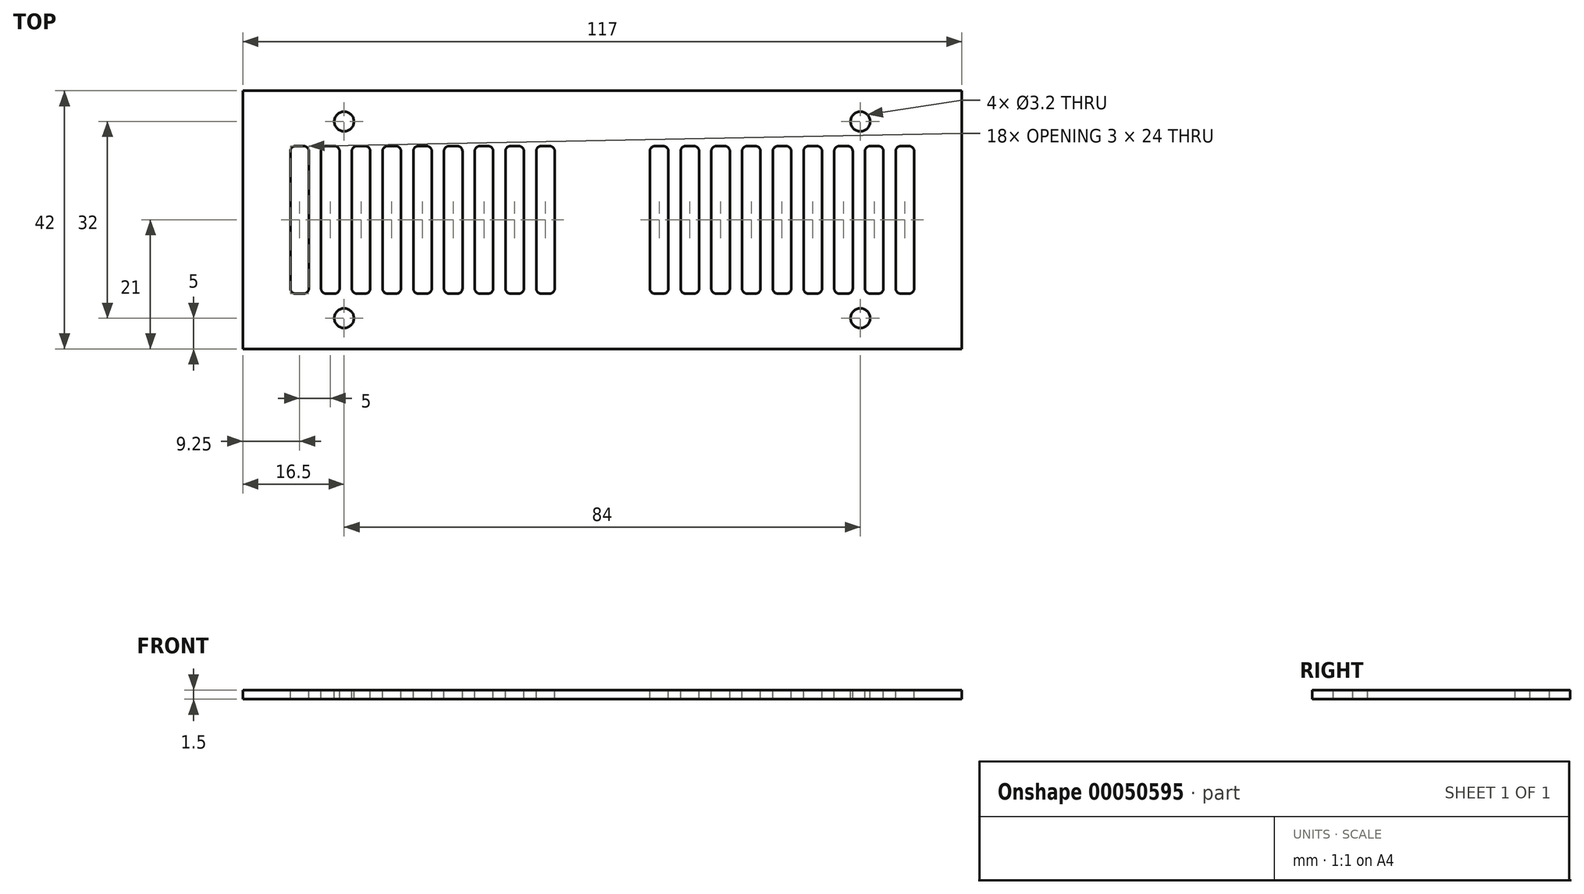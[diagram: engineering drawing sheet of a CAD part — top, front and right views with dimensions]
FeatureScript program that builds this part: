
annotation { "Feature Type Name" : "Feature", "Feature Type Description" : "" }
export const myFeature = defineFeature(function(context is Context, id is Id, definition is map)
    precondition{}
    {
        {
            var Q0;
            Q0=qCreatedBy(makeId("Top.planeOp"),FACE);
            var sketch = newSketch(context, id + "F0", { "sketchPlane" : qUnion([Q0])});
            skLineSegment(sketch, "E0.rect.bottom", {"start": v(58.5, 21) * mm, "end": v(-58.5, 21) * mm});
            skLineSegment(sketch, "E0.rect.top", {"start": v(58.5, -21) * mm, "end": v(-58.5, -21) * mm});
            skLineSegment(sketch, "E0.rect.left", {"start": v(58.5, 21) * mm, "end": v(58.5, -21) * mm});
            skLineSegment(sketch, "E0.rect.right", {"start": v(-58.5, 21) * mm, "end": v(-58.5, -21) * mm});
            skPoint(sketch, "E0.rect.middle", {"position": v(0, 0) * mm});
            skCircle(sketch, "E1", {"center": v(-42, 16) * mm, "radius": 1.6 * mm});
            skCircle(sketch, "E2", {"center": v(42, 16) * mm, "radius": 1.6 * mm});
            skCircle(sketch, "E3", {"center": v(-42, -16) * mm, "radius": 1.6 * mm});
            skCircle(sketch, "E4", {"center": v(42, -16) * mm, "radius": 1.6 * mm});
            skLineSegment(sketch, "E5.rect.bottom", {"start": v(8.55, 12) * mm, "end": v(9.95, 12) * mm});
            skLineSegment(sketch, "E5.rect.top", {"start": v(8.55, -12) * mm, "end": v(9.95, -12) * mm});
            skLineSegment(sketch, "E5.rect.left", {"start": v(7.75, 11.2) * mm, "end": v(7.75, -11.2) * mm});
            skLineSegment(sketch, "E5.rect.right", {"start": v(10.75, 11.2) * mm, "end": v(10.75, -11.2) * mm});
            skPoint(sketch, "E5.rect.middle", {"position": v(9.25, 0) * mm});
            skPoint(sketch, "E6.visualSharp", {"position": v(7.75, 12) * mm});
            skArc(sketch, "E6.filletArc", {"start": v(8.55, 12) * mm, "mid": v(7.98, 11.77) * mm, "end": v(7.75, 11.2) * mm});
            skPoint(sketch, "E7.visualSharp", {"position": v(10.75, 12) * mm});
            skArc(sketch, "E7.filletArc", {"start": v(10.75, 11.2) * mm, "mid": v(10.52, 11.77) * mm, "end": v(9.95, 12) * mm});
            skPoint(sketch, "E8.visualSharp", {"position": v(10.75, -12) * mm});
            skArc(sketch, "E8.filletArc", {"start": v(9.95, -12) * mm, "mid": v(10.52, -11.77) * mm, "end": v(10.75, -11.2) * mm});
            skPoint(sketch, "E9.visualSharp", {"position": v(7.75, -12) * mm});
            skArc(sketch, "E9.filletArc", {"start": v(7.75, -11.2) * mm, "mid": v(7.98, -11.77) * mm, "end": v(8.55, -12) * mm});
            skPoint(sketch, "E10.1.0.0", {"position": v(14.25, 0) * mm});
            skPoint(sketch, "E10.1.0.1", {"position": v(12.75, -12) * mm});
            skPoint(sketch, "E10.1.0.2", {"position": v(15.75, -12) * mm});
            skPoint(sketch, "E10.1.0.3", {"position": v(15.75, 12) * mm});
            skLineSegment(sketch, "E10.1.0.4", {"start": v(12.75, 11.2) * mm, "end": v(12.75, -11.2) * mm});
            skLineSegment(sketch, "E10.1.0.5", {"start": v(15.75, 11.2) * mm, "end": v(15.75, -11.2) * mm});
            skPoint(sketch, "E10.1.0.6", {"position": v(12.75, 12) * mm});
            skArc(sketch, "E10.1.0.7", {"start": v(12.75, -11.2) * mm, "mid": v(12.98, -11.77) * mm, "end": v(13.55, -12) * mm});
            skArc(sketch, "E10.1.0.8", {"start": v(14.95, -12) * mm, "mid": v(15.52, -11.77) * mm, "end": v(15.75, -11.2) * mm});
            skArc(sketch, "E10.1.0.9", {"start": v(15.75, 11.2) * mm, "mid": v(15.52, 11.77) * mm, "end": v(14.95, 12) * mm});
            skLineSegment(sketch, "E10.1.0.10", {"start": v(13.55, 12) * mm, "end": v(14.95, 12) * mm});
            skLineSegment(sketch, "E10.1.0.11", {"start": v(13.55, -12) * mm, "end": v(14.95, -12) * mm});
            skArc(sketch, "E10.1.0.12", {"start": v(13.55, 12) * mm, "mid": v(12.98, 11.77) * mm, "end": v(12.75, 11.2) * mm});
            skPoint(sketch, "E10.2.0.0", {"position": v(19.25, 0) * mm});
            skPoint(sketch, "E10.2.0.1", {"position": v(17.75, -12) * mm});
            skPoint(sketch, "E10.2.0.2", {"position": v(20.75, -12) * mm});
            skPoint(sketch, "E10.2.0.3", {"position": v(20.75, 12) * mm});
            skLineSegment(sketch, "E10.2.0.4", {"start": v(17.75, 11.2) * mm, "end": v(17.75, -11.2) * mm});
            skLineSegment(sketch, "E10.2.0.5", {"start": v(20.75, 11.2) * mm, "end": v(20.75, -11.2) * mm});
            skPoint(sketch, "E10.2.0.6", {"position": v(17.75, 12) * mm});
            skArc(sketch, "E10.2.0.7", {"start": v(17.75, -11.2) * mm, "mid": v(17.98, -11.77) * mm, "end": v(18.55, -12) * mm});
            skArc(sketch, "E10.2.0.8", {"start": v(19.95, -12) * mm, "mid": v(20.52, -11.77) * mm, "end": v(20.75, -11.2) * mm});
            skArc(sketch, "E10.2.0.9", {"start": v(20.75, 11.2) * mm, "mid": v(20.52, 11.77) * mm, "end": v(19.95, 12) * mm});
            skLineSegment(sketch, "E10.2.0.10", {"start": v(18.55, 12) * mm, "end": v(19.95, 12) * mm});
            skLineSegment(sketch, "E10.2.0.11", {"start": v(18.55, -12) * mm, "end": v(19.95, -12) * mm});
            skArc(sketch, "E10.2.0.12", {"start": v(18.55, 12) * mm, "mid": v(17.98, 11.77) * mm, "end": v(17.75, 11.2) * mm});
            skPoint(sketch, "E10.3.0.0", {"position": v(24.25, 0) * mm});
            skPoint(sketch, "E10.3.0.1", {"position": v(22.75, -12) * mm});
            skPoint(sketch, "E10.3.0.2", {"position": v(25.75, -12) * mm});
            skPoint(sketch, "E10.3.0.3", {"position": v(25.75, 12) * mm});
            skLineSegment(sketch, "E10.3.0.4", {"start": v(22.75, 11.2) * mm, "end": v(22.75, -11.2) * mm});
            skLineSegment(sketch, "E10.3.0.5", {"start": v(25.75, 11.2) * mm, "end": v(25.75, -11.2) * mm});
            skPoint(sketch, "E10.3.0.6", {"position": v(22.75, 12) * mm});
            skArc(sketch, "E10.3.0.7", {"start": v(22.75, -11.2) * mm, "mid": v(22.98, -11.77) * mm, "end": v(23.55, -12) * mm});
            skArc(sketch, "E10.3.0.8", {"start": v(24.95, -12) * mm, "mid": v(25.52, -11.77) * mm, "end": v(25.75, -11.2) * mm});
            skArc(sketch, "E10.3.0.9", {"start": v(25.75, 11.2) * mm, "mid": v(25.52, 11.77) * mm, "end": v(24.95, 12) * mm});
            skLineSegment(sketch, "E10.3.0.10", {"start": v(23.55, 12) * mm, "end": v(24.95, 12) * mm});
            skLineSegment(sketch, "E10.3.0.11", {"start": v(23.55, -12) * mm, "end": v(24.95, -12) * mm});
            skArc(sketch, "E10.3.0.12", {"start": v(23.55, 12) * mm, "mid": v(22.98, 11.77) * mm, "end": v(22.75, 11.2) * mm});
            skPoint(sketch, "E10.4.0.0", {"position": v(29.25, 0) * mm});
            skPoint(sketch, "E10.4.0.1", {"position": v(27.75, -12) * mm});
            skPoint(sketch, "E10.4.0.2", {"position": v(30.75, -12) * mm});
            skPoint(sketch, "E10.4.0.3", {"position": v(30.75, 12) * mm});
            skLineSegment(sketch, "E10.4.0.4", {"start": v(27.75, 11.2) * mm, "end": v(27.75, -11.2) * mm});
            skLineSegment(sketch, "E10.4.0.5", {"start": v(30.75, 11.2) * mm, "end": v(30.75, -11.2) * mm});
            skPoint(sketch, "E10.4.0.6", {"position": v(27.75, 12) * mm});
            skArc(sketch, "E10.4.0.7", {"start": v(27.75, -11.2) * mm, "mid": v(27.98, -11.77) * mm, "end": v(28.55, -12) * mm});
            skArc(sketch, "E10.4.0.8", {"start": v(29.95, -12) * mm, "mid": v(30.52, -11.77) * mm, "end": v(30.75, -11.2) * mm});
            skArc(sketch, "E10.4.0.9", {"start": v(30.75, 11.2) * mm, "mid": v(30.52, 11.77) * mm, "end": v(29.95, 12) * mm});
            skLineSegment(sketch, "E10.4.0.10", {"start": v(28.55, 12) * mm, "end": v(29.95, 12) * mm});
            skLineSegment(sketch, "E10.4.0.11", {"start": v(28.55, -12) * mm, "end": v(29.95, -12) * mm});
            skArc(sketch, "E10.4.0.12", {"start": v(28.55, 12) * mm, "mid": v(27.98, 11.77) * mm, "end": v(27.75, 11.2) * mm});
            skPoint(sketch, "E10.5.0.0", {"position": v(34.25, 0) * mm});
            skPoint(sketch, "E10.5.0.1", {"position": v(32.75, -12) * mm});
            skPoint(sketch, "E10.5.0.2", {"position": v(35.75, -12) * mm});
            skPoint(sketch, "E10.5.0.3", {"position": v(35.75, 12) * mm});
            skLineSegment(sketch, "E10.5.0.4", {"start": v(32.75, 11.2) * mm, "end": v(32.75, -11.2) * mm});
            skLineSegment(sketch, "E10.5.0.5", {"start": v(35.75, 11.2) * mm, "end": v(35.75, -11.2) * mm});
            skPoint(sketch, "E10.5.0.6", {"position": v(32.75, 12) * mm});
            skArc(sketch, "E10.5.0.7", {"start": v(32.75, -11.2) * mm, "mid": v(32.98, -11.77) * mm, "end": v(33.55, -12) * mm});
            skArc(sketch, "E10.5.0.8", {"start": v(34.95, -12) * mm, "mid": v(35.52, -11.77) * mm, "end": v(35.75, -11.2) * mm});
            skArc(sketch, "E10.5.0.9", {"start": v(35.75, 11.2) * mm, "mid": v(35.52, 11.77) * mm, "end": v(34.95, 12) * mm});
            skLineSegment(sketch, "E10.5.0.10", {"start": v(33.55, 12) * mm, "end": v(34.95, 12) * mm});
            skLineSegment(sketch, "E10.5.0.11", {"start": v(33.55, -12) * mm, "end": v(34.95, -12) * mm});
            skArc(sketch, "E10.5.0.12", {"start": v(33.55, 12) * mm, "mid": v(32.98, 11.77) * mm, "end": v(32.75, 11.2) * mm});
            skPoint(sketch, "E10.6.0.0", {"position": v(39.25, 0) * mm});
            skPoint(sketch, "E10.6.0.1", {"position": v(37.75, -12) * mm});
            skPoint(sketch, "E10.6.0.2", {"position": v(40.75, -12) * mm});
            skPoint(sketch, "E10.6.0.3", {"position": v(40.75, 12) * mm});
            skLineSegment(sketch, "E10.6.0.4", {"start": v(37.75, 11.2) * mm, "end": v(37.75, -11.2) * mm});
            skLineSegment(sketch, "E10.6.0.5", {"start": v(40.75, 11.2) * mm, "end": v(40.75, -11.2) * mm});
            skPoint(sketch, "E10.6.0.6", {"position": v(37.75, 12) * mm});
            skArc(sketch, "E10.6.0.7", {"start": v(37.75, -11.2) * mm, "mid": v(37.98, -11.77) * mm, "end": v(38.55, -12) * mm});
            skArc(sketch, "E10.6.0.8", {"start": v(39.95, -12) * mm, "mid": v(40.52, -11.77) * mm, "end": v(40.75, -11.2) * mm});
            skArc(sketch, "E10.6.0.9", {"start": v(40.75, 11.2) * mm, "mid": v(40.52, 11.77) * mm, "end": v(39.95, 12) * mm});
            skLineSegment(sketch, "E10.6.0.10", {"start": v(38.55, 12) * mm, "end": v(39.95, 12) * mm});
            skLineSegment(sketch, "E10.6.0.11", {"start": v(38.55, -12) * mm, "end": v(39.95, -12) * mm});
            skArc(sketch, "E10.6.0.12", {"start": v(38.55, 12) * mm, "mid": v(37.98, 11.77) * mm, "end": v(37.75, 11.2) * mm});
            skPoint(sketch, "E10.7.0.0", {"position": v(44.25, 0) * mm});
            skPoint(sketch, "E10.7.0.1", {"position": v(42.75, -12) * mm});
            skPoint(sketch, "E10.7.0.2", {"position": v(45.75, -12) * mm});
            skPoint(sketch, "E10.7.0.3", {"position": v(45.75, 12) * mm});
            skLineSegment(sketch, "E10.7.0.4", {"start": v(42.75, 11.2) * mm, "end": v(42.75, -11.2) * mm});
            skLineSegment(sketch, "E10.7.0.5", {"start": v(45.75, 11.2) * mm, "end": v(45.75, -11.2) * mm});
            skPoint(sketch, "E10.7.0.6", {"position": v(42.75, 12) * mm});
            skArc(sketch, "E10.7.0.7", {"start": v(42.75, -11.2) * mm, "mid": v(42.98, -11.77) * mm, "end": v(43.55, -12) * mm});
            skArc(sketch, "E10.7.0.8", {"start": v(44.95, -12) * mm, "mid": v(45.52, -11.77) * mm, "end": v(45.75, -11.2) * mm});
            skArc(sketch, "E10.7.0.9", {"start": v(45.75, 11.2) * mm, "mid": v(45.52, 11.77) * mm, "end": v(44.95, 12) * mm});
            skLineSegment(sketch, "E10.7.0.10", {"start": v(43.55, 12) * mm, "end": v(44.95, 12) * mm});
            skLineSegment(sketch, "E10.7.0.11", {"start": v(43.55, -12) * mm, "end": v(44.95, -12) * mm});
            skArc(sketch, "E10.7.0.12", {"start": v(43.55, 12) * mm, "mid": v(42.98, 11.77) * mm, "end": v(42.75, 11.2) * mm});
            skPoint(sketch, "E10.8.0.0", {"position": v(49.25, 0) * mm});
            skPoint(sketch, "E10.8.0.1", {"position": v(47.75, -12) * mm});
            skPoint(sketch, "E10.8.0.2", {"position": v(50.75, -12) * mm});
            skPoint(sketch, "E10.8.0.3", {"position": v(50.75, 12) * mm});
            skLineSegment(sketch, "E10.8.0.4", {"start": v(47.75, 11.2) * mm, "end": v(47.75, -11.2) * mm});
            skLineSegment(sketch, "E10.8.0.5", {"start": v(50.75, 11.2) * mm, "end": v(50.75, -11.2) * mm});
            skPoint(sketch, "E10.8.0.6", {"position": v(47.75, 12) * mm});
            skArc(sketch, "E10.8.0.7", {"start": v(47.75, -11.2) * mm, "mid": v(47.98, -11.77) * mm, "end": v(48.55, -12) * mm});
            skArc(sketch, "E10.8.0.8", {"start": v(49.95, -12) * mm, "mid": v(50.52, -11.77) * mm, "end": v(50.75, -11.2) * mm});
            skArc(sketch, "E10.8.0.9", {"start": v(50.75, 11.2) * mm, "mid": v(50.52, 11.77) * mm, "end": v(49.95, 12) * mm});
            skLineSegment(sketch, "E10.8.0.10", {"start": v(48.55, 12) * mm, "end": v(49.95, 12) * mm});
            skLineSegment(sketch, "E10.8.0.11", {"start": v(48.55, -12) * mm, "end": v(49.95, -12) * mm});
            skArc(sketch, "E10.8.0.12", {"start": v(48.55, 12) * mm, "mid": v(47.98, 11.77) * mm, "end": v(47.75, 11.2) * mm});
            skLineSegment(sketch, "E10.direction1", {"start": v(9.25, 0) * mm, "end": v(14.25, 0) * mm, "construction": true});
            skLineSegment(sketch, "E11.rect.bottom", {"start": v(-49.95, 12) * mm, "end": v(-48.55, 12) * mm});
            skLineSegment(sketch, "E11.rect.top", {"start": v(-49.95, -12) * mm, "end": v(-48.55, -12) * mm});
            skLineSegment(sketch, "E11.rect.left", {"start": v(-50.75, 11.2) * mm, "end": v(-50.75, -11.2) * mm});
            skLineSegment(sketch, "E11.rect.right", {"start": v(-47.75, 11.2) * mm, "end": v(-47.75, -11.2) * mm});
            skPoint(sketch, "E11.rect.middle", {"position": v(-49.25, 0) * mm});
            skPoint(sketch, "E12.visualSharp", {"position": v(-50.75, 12) * mm});
            skArc(sketch, "E12.filletArc", {"start": v(-49.95, 12) * mm, "mid": v(-50.52, 11.77) * mm, "end": v(-50.75, 11.2) * mm});
            skPoint(sketch, "E13.visualSharp", {"position": v(-47.75, 12) * mm});
            skArc(sketch, "E13.filletArc", {"start": v(-47.75, 11.2) * mm, "mid": v(-47.98, 11.77) * mm, "end": v(-48.55, 12) * mm});
            skPoint(sketch, "E14.visualSharp", {"position": v(-47.75, -12) * mm});
            skArc(sketch, "E14.filletArc", {"start": v(-48.55, -12) * mm, "mid": v(-47.98, -11.77) * mm, "end": v(-47.75, -11.2) * mm});
            skPoint(sketch, "E15.visualSharp", {"position": v(-50.75, -12) * mm});
            skArc(sketch, "E15.filletArc", {"start": v(-50.75, -11.2) * mm, "mid": v(-50.52, -11.77) * mm, "end": v(-49.95, -12) * mm});
            skPoint(sketch, "E16.1.0.0", {"position": v(-42.75, 12) * mm});
            skPoint(sketch, "E16.1.0.1", {"position": v(-42.75, -12) * mm});
            skLineSegment(sketch, "E16.1.0.2", {"start": v(-42.75, 11.2) * mm, "end": v(-42.75, -11.2) * mm});
            skLineSegment(sketch, "E16.1.0.3", {"start": v(-45.75, 11.2) * mm, "end": v(-45.75, -11.2) * mm});
            skPoint(sketch, "E16.1.0.4", {"position": v(-45.75, -12) * mm});
            skPoint(sketch, "E16.1.0.5", {"position": v(-44.25, 0) * mm});
            skPoint(sketch, "E16.1.0.6", {"position": v(-45.75, 12) * mm});
            skArc(sketch, "E16.1.0.7", {"start": v(-44.95, 12) * mm, "mid": v(-45.52, 11.77) * mm, "end": v(-45.75, 11.2) * mm});
            skArc(sketch, "E16.1.0.8", {"start": v(-45.75, -11.2) * mm, "mid": v(-45.52, -11.77) * mm, "end": v(-44.95, -12) * mm});
            skLineSegment(sketch, "E16.1.0.9", {"start": v(-44.95, 12) * mm, "end": v(-43.55, 12) * mm});
            skLineSegment(sketch, "E16.1.0.10", {"start": v(-44.95, -12) * mm, "end": v(-43.55, -12) * mm});
            skArc(sketch, "E16.1.0.11", {"start": v(-42.75, 11.2) * mm, "mid": v(-42.98, 11.77) * mm, "end": v(-43.55, 12) * mm});
            skArc(sketch, "E16.1.0.12", {"start": v(-43.55, -12) * mm, "mid": v(-42.98, -11.77) * mm, "end": v(-42.75, -11.2) * mm});
            skPoint(sketch, "E16.2.0.0", {"position": v(-37.75, 12) * mm});
            skPoint(sketch, "E16.2.0.1", {"position": v(-37.75, -12) * mm});
            skLineSegment(sketch, "E16.2.0.2", {"start": v(-37.75, 11.2) * mm, "end": v(-37.75, -11.2) * mm});
            skLineSegment(sketch, "E16.2.0.3", {"start": v(-40.75, 11.2) * mm, "end": v(-40.75, -11.2) * mm});
            skPoint(sketch, "E16.2.0.4", {"position": v(-40.75, -12) * mm});
            skPoint(sketch, "E16.2.0.5", {"position": v(-39.25, 0) * mm});
            skPoint(sketch, "E16.2.0.6", {"position": v(-40.75, 12) * mm});
            skArc(sketch, "E16.2.0.7", {"start": v(-39.95, 12) * mm, "mid": v(-40.52, 11.77) * mm, "end": v(-40.75, 11.2) * mm});
            skArc(sketch, "E16.2.0.8", {"start": v(-40.75, -11.2) * mm, "mid": v(-40.52, -11.77) * mm, "end": v(-39.95, -12) * mm});
            skLineSegment(sketch, "E16.2.0.9", {"start": v(-39.95, 12) * mm, "end": v(-38.55, 12) * mm});
            skLineSegment(sketch, "E16.2.0.10", {"start": v(-39.95, -12) * mm, "end": v(-38.55, -12) * mm});
            skArc(sketch, "E16.2.0.11", {"start": v(-37.75, 11.2) * mm, "mid": v(-37.98, 11.77) * mm, "end": v(-38.55, 12) * mm});
            skArc(sketch, "E16.2.0.12", {"start": v(-38.55, -12) * mm, "mid": v(-37.98, -11.77) * mm, "end": v(-37.75, -11.2) * mm});
            skPoint(sketch, "E16.3.0.0", {"position": v(-32.75, 12) * mm});
            skPoint(sketch, "E16.3.0.1", {"position": v(-32.75, -12) * mm});
            skLineSegment(sketch, "E16.3.0.2", {"start": v(-32.75, 11.2) * mm, "end": v(-32.75, -11.2) * mm});
            skLineSegment(sketch, "E16.3.0.3", {"start": v(-35.75, 11.2) * mm, "end": v(-35.75, -11.2) * mm});
            skPoint(sketch, "E16.3.0.4", {"position": v(-35.75, -12) * mm});
            skPoint(sketch, "E16.3.0.5", {"position": v(-34.25, 0) * mm});
            skPoint(sketch, "E16.3.0.6", {"position": v(-35.75, 12) * mm});
            skArc(sketch, "E16.3.0.7", {"start": v(-34.95, 12) * mm, "mid": v(-35.52, 11.77) * mm, "end": v(-35.75, 11.2) * mm});
            skArc(sketch, "E16.3.0.8", {"start": v(-35.75, -11.2) * mm, "mid": v(-35.52, -11.77) * mm, "end": v(-34.95, -12) * mm});
            skLineSegment(sketch, "E16.3.0.9", {"start": v(-34.95, 12) * mm, "end": v(-33.55, 12) * mm});
            skLineSegment(sketch, "E16.3.0.10", {"start": v(-34.95, -12) * mm, "end": v(-33.55, -12) * mm});
            skArc(sketch, "E16.3.0.11", {"start": v(-32.75, 11.2) * mm, "mid": v(-32.98, 11.77) * mm, "end": v(-33.55, 12) * mm});
            skArc(sketch, "E16.3.0.12", {"start": v(-33.55, -12) * mm, "mid": v(-32.98, -11.77) * mm, "end": v(-32.75, -11.2) * mm});
            skPoint(sketch, "E16.4.0.0", {"position": v(-27.75, 12) * mm});
            skPoint(sketch, "E16.4.0.1", {"position": v(-27.75, -12) * mm});
            skLineSegment(sketch, "E16.4.0.2", {"start": v(-27.75, 11.2) * mm, "end": v(-27.75, -11.2) * mm});
            skLineSegment(sketch, "E16.4.0.3", {"start": v(-30.75, 11.2) * mm, "end": v(-30.75, -11.2) * mm});
            skPoint(sketch, "E16.4.0.4", {"position": v(-30.75, -12) * mm});
            skPoint(sketch, "E16.4.0.5", {"position": v(-29.25, 0) * mm});
            skPoint(sketch, "E16.4.0.6", {"position": v(-30.75, 12) * mm});
            skArc(sketch, "E16.4.0.7", {"start": v(-29.95, 12) * mm, "mid": v(-30.52, 11.77) * mm, "end": v(-30.75, 11.2) * mm});
            skArc(sketch, "E16.4.0.8", {"start": v(-30.75, -11.2) * mm, "mid": v(-30.52, -11.77) * mm, "end": v(-29.95, -12) * mm});
            skLineSegment(sketch, "E16.4.0.9", {"start": v(-29.95, 12) * mm, "end": v(-28.55, 12) * mm});
            skLineSegment(sketch, "E16.4.0.10", {"start": v(-29.95, -12) * mm, "end": v(-28.55, -12) * mm});
            skArc(sketch, "E16.4.0.11", {"start": v(-27.75, 11.2) * mm, "mid": v(-27.98, 11.77) * mm, "end": v(-28.55, 12) * mm});
            skArc(sketch, "E16.4.0.12", {"start": v(-28.55, -12) * mm, "mid": v(-27.98, -11.77) * mm, "end": v(-27.75, -11.2) * mm});
            skPoint(sketch, "E16.5.0.0", {"position": v(-22.75, 12) * mm});
            skPoint(sketch, "E16.5.0.1", {"position": v(-22.75, -12) * mm});
            skLineSegment(sketch, "E16.5.0.2", {"start": v(-22.75, 11.2) * mm, "end": v(-22.75, -11.2) * mm});
            skLineSegment(sketch, "E16.5.0.3", {"start": v(-25.75, 11.2) * mm, "end": v(-25.75, -11.2) * mm});
            skPoint(sketch, "E16.5.0.4", {"position": v(-25.75, -12) * mm});
            skPoint(sketch, "E16.5.0.5", {"position": v(-24.25, 0) * mm});
            skPoint(sketch, "E16.5.0.6", {"position": v(-25.75, 12) * mm});
            skArc(sketch, "E16.5.0.7", {"start": v(-24.95, 12) * mm, "mid": v(-25.52, 11.77) * mm, "end": v(-25.75, 11.2) * mm});
            skArc(sketch, "E16.5.0.8", {"start": v(-25.75, -11.2) * mm, "mid": v(-25.52, -11.77) * mm, "end": v(-24.95, -12) * mm});
            skLineSegment(sketch, "E16.5.0.9", {"start": v(-24.95, 12) * mm, "end": v(-23.55, 12) * mm});
            skLineSegment(sketch, "E16.5.0.10", {"start": v(-24.95, -12) * mm, "end": v(-23.55, -12) * mm});
            skArc(sketch, "E16.5.0.11", {"start": v(-22.75, 11.2) * mm, "mid": v(-22.98, 11.77) * mm, "end": v(-23.55, 12) * mm});
            skArc(sketch, "E16.5.0.12", {"start": v(-23.55, -12) * mm, "mid": v(-22.98, -11.77) * mm, "end": v(-22.75, -11.2) * mm});
            skPoint(sketch, "E16.6.0.0", {"position": v(-17.75, 12) * mm});
            skPoint(sketch, "E16.6.0.1", {"position": v(-17.75, -12) * mm});
            skLineSegment(sketch, "E16.6.0.2", {"start": v(-17.75, 11.2) * mm, "end": v(-17.75, -11.2) * mm});
            skLineSegment(sketch, "E16.6.0.3", {"start": v(-20.75, 11.2) * mm, "end": v(-20.75, -11.2) * mm});
            skPoint(sketch, "E16.6.0.4", {"position": v(-20.75, -12) * mm});
            skPoint(sketch, "E16.6.0.5", {"position": v(-19.25, 0) * mm});
            skPoint(sketch, "E16.6.0.6", {"position": v(-20.75, 12) * mm});
            skArc(sketch, "E16.6.0.7", {"start": v(-19.95, 12) * mm, "mid": v(-20.52, 11.77) * mm, "end": v(-20.75, 11.2) * mm});
            skArc(sketch, "E16.6.0.8", {"start": v(-20.75, -11.2) * mm, "mid": v(-20.52, -11.77) * mm, "end": v(-19.95, -12) * mm});
            skLineSegment(sketch, "E16.6.0.9", {"start": v(-19.95, 12) * mm, "end": v(-18.55, 12) * mm});
            skLineSegment(sketch, "E16.6.0.10", {"start": v(-19.95, -12) * mm, "end": v(-18.55, -12) * mm});
            skArc(sketch, "E16.6.0.11", {"start": v(-17.75, 11.2) * mm, "mid": v(-17.98, 11.77) * mm, "end": v(-18.55, 12) * mm});
            skArc(sketch, "E16.6.0.12", {"start": v(-18.55, -12) * mm, "mid": v(-17.98, -11.77) * mm, "end": v(-17.75, -11.2) * mm});
            skPoint(sketch, "E16.7.0.0", {"position": v(-12.75, 12) * mm});
            skPoint(sketch, "E16.7.0.1", {"position": v(-12.75, -12) * mm});
            skLineSegment(sketch, "E16.7.0.2", {"start": v(-12.75, 11.2) * mm, "end": v(-12.75, -11.2) * mm});
            skLineSegment(sketch, "E16.7.0.3", {"start": v(-15.75, 11.2) * mm, "end": v(-15.75, -11.2) * mm});
            skPoint(sketch, "E16.7.0.4", {"position": v(-15.75, -12) * mm});
            skPoint(sketch, "E16.7.0.5", {"position": v(-14.25, 0) * mm});
            skPoint(sketch, "E16.7.0.6", {"position": v(-15.75, 12) * mm});
            skArc(sketch, "E16.7.0.7", {"start": v(-14.95, 12) * mm, "mid": v(-15.52, 11.77) * mm, "end": v(-15.75, 11.2) * mm});
            skArc(sketch, "E16.7.0.8", {"start": v(-15.75, -11.2) * mm, "mid": v(-15.52, -11.77) * mm, "end": v(-14.95, -12) * mm});
            skLineSegment(sketch, "E16.7.0.9", {"start": v(-14.95, 12) * mm, "end": v(-13.55, 12) * mm});
            skLineSegment(sketch, "E16.7.0.10", {"start": v(-14.95, -12) * mm, "end": v(-13.55, -12) * mm});
            skArc(sketch, "E16.7.0.11", {"start": v(-12.75, 11.2) * mm, "mid": v(-12.98, 11.77) * mm, "end": v(-13.55, 12) * mm});
            skArc(sketch, "E16.7.0.12", {"start": v(-13.55, -12) * mm, "mid": v(-12.98, -11.77) * mm, "end": v(-12.75, -11.2) * mm});
            skPoint(sketch, "E16.8.0.0", {"position": v(-7.75, 12) * mm});
            skPoint(sketch, "E16.8.0.1", {"position": v(-7.75, -12) * mm});
            skLineSegment(sketch, "E16.8.0.2", {"start": v(-7.75, 11.2) * mm, "end": v(-7.75, -11.2) * mm});
            skLineSegment(sketch, "E16.8.0.3", {"start": v(-10.75, 11.2) * mm, "end": v(-10.75, -11.2) * mm});
            skPoint(sketch, "E16.8.0.4", {"position": v(-10.75, -12) * mm});
            skPoint(sketch, "E16.8.0.5", {"position": v(-9.25, 0) * mm});
            skPoint(sketch, "E16.8.0.6", {"position": v(-10.75, 12) * mm});
            skArc(sketch, "E16.8.0.7", {"start": v(-9.95, 12) * mm, "mid": v(-10.52, 11.77) * mm, "end": v(-10.75, 11.2) * mm});
            skArc(sketch, "E16.8.0.8", {"start": v(-10.75, -11.2) * mm, "mid": v(-10.52, -11.77) * mm, "end": v(-9.95, -12) * mm});
            skLineSegment(sketch, "E16.8.0.9", {"start": v(-9.95, 12) * mm, "end": v(-8.55, 12) * mm});
            skLineSegment(sketch, "E16.8.0.10", {"start": v(-9.95, -12) * mm, "end": v(-8.55, -12) * mm});
            skArc(sketch, "E16.8.0.11", {"start": v(-7.75, 11.2) * mm, "mid": v(-7.98, 11.77) * mm, "end": v(-8.55, 12) * mm});
            skArc(sketch, "E16.8.0.12", {"start": v(-8.55, -12) * mm, "mid": v(-7.98, -11.77) * mm, "end": v(-7.75, -11.2) * mm});
            skLineSegment(sketch, "E16.direction1", {"start": v(-47.75, 12) * mm, "end": v(-42.75, 12) * mm, "construction": true});
            skSolve(sketch);
        }
        {
            var Q0;
            Q0=makeQuery(id+"F0.imprint","IMPRINT",FACE,{"disambiguationData":[TD([[makeQuery(id+"F0.imprint","IMPRINT",EDGE,{"derivedFrom":sQuery(id+"F0.wireOp",EDGE,"E0.rect.bottom")}),1.0]])]});
            extrude(context, id + "F1", {"entities" : qUnion([Q0]), "oppositeDirection" : true, "depth" : 1.5 * mm});
        }
    });
